# Revit family: RN 17011 Schrägfilter
name_source: partatom
category: Rohrzubehör
units: mm (PartAtom-declared; Revit-internal decimal feet)

## family parameters
Arbeitsebenenbasiert = Nein
Beim Laden mit Abzugskörper schneiden = Nein
Bemaßung runder Anschluss = Durchmesser verwenden
Gemeinsam genutzt = Nein
Immer vertikal = Ja
Teiletyp = Ventil - Zerlegung in

## types (7) — shared parameters
1.010.00.2 Blattnummer der Richtlinie = 17
1.010.00.3 Ausgabedatum (Monat) der Richtlinie = 201601
1.010.00.4 Herstellername = R. Nussbaum AG
1.010.00.5 Revisionsdatum der Datei = 20190528
1.010.00.6 Webadresse des Herstellers = http://www.nussbaum.ch
1.100.00.3 Sortiernummer für Anzeigereihenfolge = 9
1.100.00.4 Produktbezeichnung = Filterkombination, Filter und Schmutzfänger
1.960/3L.00.8 Link (URL) = https://www.nussbaum.ch
17.700.00.4 Armaturentyp = 1
17.700.00.7 Maximale Betriebstemperatur TB [°C] = 60
17.700.00.8 Maximaler Betriebsdruck (Arbeitsdruck) ps [1.0 · 105 Pa] = 16
Connector Visibility = Nein
EnclosingSpace Visibility = Nein
Hersteller = R. Nussbauzm AG
URL = https://www.nussbaum.ch

## per-type parameters (varying)
- DN 10: 1.800.00.3 TGA-Nummer=0090030000000000000000000000020070000000000000000100000000; 1.810.00.3 Hersteller-Bestellnummer=17011.03; 1.810.00.4 DATANORM-Nummer=17011.03; 1.810.00.5 StLB-Nummer=616.132; 1.810.00.6 GTIN-Nummer=7612945612618; 17.700.00.30 Produktbeschreibung=17011.03, Schrägfilter, DN=10, Rp=3/8; 17.700.00.5 Nennweite DN=10; 17.700.00.6 kvs-Wert [m3/h]=3; CONNECTOR0_DIAMETER_dX_0r=15 mm; CONNECTOR0_dX_00=35 mm; CONNECTOR0_dX_01=22 mm; CONNECTOR0_ref_dX=22 mm; CONNECTOR1_DIAMETER_dX_0r=15 mm; CONNECTOR1_dX_00=22 mm; CONNECTOR1_dX_01=35 mm; CONNECTOR1_ref_dX=22 mm; Modell=17011.03; R. Nussbaum AG 17011.03 de Visibility=Ja; R. Nussbaum AG 17011.04 de Visibility=Nein; R. Nussbaum AG 17011.05 de Visibility=Nein; R. Nussbaum AG 17011.06 de Visibility=Nein; R. Nussbaum AG 17011.07 de Visibility=Nein; R. Nussbaum AG 17011.08 de Visibility=Nein; R. Nussbaum AG 17011.09 de Visibility=Nein; Typenkommentare=SchrägfilterDN 10
- DN 15: 1.800.00.3 TGA-Nummer=0090030000000000000000000000020070000000000000000200000000; 1.810.00.3 Hersteller-Bestellnummer=17011.04; 1.810.00.4 DATANORM-Nummer=17011.04; 1.810.00.5 StLB-Nummer=616.133; 1.810.00.6 GTIN-Nummer=7612945612625; 17.700.00.30 Produktbeschreibung=17011.04, Schrägfilter, DN=15, Rp=½; 17.700.00.5 Nennweite DN=15; 17.700.00.6 kvs-Wert [m3/h]=6.3; CONNECTOR0_DIAMETER_dX_0r=15 mm; CONNECTOR0_dX_00=35 mm; CONNECTOR0_dX_01=22 mm; CONNECTOR0_ref_dX=22 mm; CONNECTOR1_DIAMETER_dX_0r=15 mm; CONNECTOR1_dX_00=22 mm; CONNECTOR1_dX_01=35 mm; CONNECTOR1_ref_dX=22 mm; Modell=17011.04; R. Nussbaum AG 17011.03 de Visibility=Nein; R. Nussbaum AG 17011.04 de Visibility=Ja; R. Nussbaum AG 17011.05 de Visibility=Nein; R. Nussbaum AG 17011.06 de Visibility=Nein; R. Nussbaum AG 17011.07 de Visibility=Nein; R. Nussbaum AG 17011.08 de Visibility=Nein; R. Nussbaum AG 17011.09 de Visibility=Nein; Typenkommentare=SchrägfilterDN 15
- DN 20: 1.800.00.3 TGA-Nummer=0090030000000000000000000000020070000000000000000300000000; 1.810.00.3 Hersteller-Bestellnummer=17011.05; 1.810.00.4 DATANORM-Nummer=17011.05; 1.810.00.5 StLB-Nummer=616.134; 1.810.00.6 GTIN-Nummer=7612945612632; 17.700.00.30 Produktbeschreibung=17011.05, Schrägfilter, DN=20, Rp=¾; 17.700.00.5 Nennweite DN=20; 17.700.00.6 kvs-Wert [m3/h]=13.4; CONNECTOR0_DIAMETER_dX_0r=20 mm; CONNECTOR0_dX_00=42 mm; CONNECTOR0_dX_01=27 mm; CONNECTOR0_ref_dX=27 mm; CONNECTOR1_DIAMETER_dX_0r=20 mm; CONNECTOR1_dX_00=28 mm; CONNECTOR1_dX_01=43 mm; CONNECTOR1_ref_dX=28 mm; Modell=17011.05; R. Nussbaum AG 17011.03 de Visibility=Nein; R. Nussbaum AG 17011.04 de Visibility=Nein; R. Nussbaum AG 17011.05 de Visibility=Ja; R. Nussbaum AG 17011.06 de Visibility=Nein; R. Nussbaum AG 17011.07 de Visibility=Nein; R. Nussbaum AG 17011.08 de Visibility=Nein; R. Nussbaum AG 17011.09 de Visibility=Nein; Typenkommentare=SchrägfilterDN 20
- DN 25: 1.800.00.3 TGA-Nummer=0090030000000000000000000000020070000000000000000400000000; 1.810.00.3 Hersteller-Bestellnummer=17011.06; 1.810.00.4 DATANORM-Nummer=17011.06; 1.810.00.5 StLB-Nummer=616.135; 1.810.00.6 GTIN-Nummer=7612945612649; 17.700.00.30 Produktbeschreibung=17011.06, Schrägfilter, DN=25, Rp=1; 17.700.00.5 Nennweite DN=25; 17.700.00.6 kvs-Wert [m3/h]=21.6; CONNECTOR0_DIAMETER_dX_0r=25 mm  [stored 0.082021 ft]; CONNECTOR0_dX_00=50 mm; CONNECTOR0_dX_01=33 mm; CONNECTOR0_ref_dX=33 mm; CONNECTOR1_DIAMETER_dX_0r=25 mm  [stored 0.082021 ft]; CONNECTOR1_dX_00=33 mm; CONNECTOR1_dX_01=50 mm; CONNECTOR1_ref_dX=33 mm; Modell=17011.06; R. Nussbaum AG 17011.03 de Visibility=Nein; R. Nussbaum AG 17011.04 de Visibility=Nein; R. Nussbaum AG 17011.05 de Visibility=Nein; R. Nussbaum AG 17011.06 de Visibility=Ja; R. Nussbaum AG 17011.07 de Visibility=Nein; R. Nussbaum AG 17011.08 de Visibility=Nein; R. Nussbaum AG 17011.09 de Visibility=Nein; Typenkommentare=SchrägfilterDN 25
- DN 32: 1.800.00.3 TGA-Nummer=0090030000000000000000000000020070000000000000000500000000; 1.810.00.3 Hersteller-Bestellnummer=17011.07; 1.810.00.4 DATANORM-Nummer=17011.07; 1.810.00.5 StLB-Nummer=616.136; 1.810.00.6 GTIN-Nummer=7612945612656; 17.700.00.30 Produktbeschreibung=17011.07, Schrägfilter, DN=32, Rp=1¼; 17.700.00.5 Nennweite DN=32; 17.700.00.6 kvs-Wert [m3/h]=37; CONNECTOR0_DIAMETER_dX_0r=32 mm; CONNECTOR0_dX_00=57 mm; CONNECTOR0_dX_01=39 mm; CONNECTOR0_ref_dX=39 mm; CONNECTOR1_DIAMETER_dX_0r=32 mm; CONNECTOR1_dX_00=38 mm; CONNECTOR1_dX_01=58 mm; CONNECTOR1_ref_dX=38 mm; Modell=17011.07; R. Nussbaum AG 17011.03 de Visibility=Nein; R. Nussbaum AG 17011.04 de Visibility=Nein; R. Nussbaum AG 17011.05 de Visibility=Nein; R. Nussbaum AG 17011.06 de Visibility=Nein; R. Nussbaum AG 17011.07 de Visibility=Ja; R. Nussbaum AG 17011.08 de Visibility=Nein; R. Nussbaum AG 17011.09 de Visibility=Nein; Typenkommentare=SchrägfilterDN 32
- DN 40: 1.800.00.3 TGA-Nummer=0090030000000000000000000000020070000000000000000600000000; 1.810.00.3 Hersteller-Bestellnummer=17011.08; 1.810.00.4 DATANORM-Nummer=17011.08; 1.810.00.5 StLB-Nummer=616.137; 1.810.00.6 GTIN-Nummer=7612945612663; 17.700.00.30 Produktbeschreibung=17011.08, Schrägfilter, DN=40, Rp=1½; 17.700.00.5 Nennweite DN=40; 17.700.00.6 kvs-Wert [m3/h]=51.6; CONNECTOR0_DIAMETER_dX_0r=40 mm; CONNECTOR0_dX_00=65 mm; CONNECTOR0_dX_01=46 mm; CONNECTOR0_ref_dX=46 mm; CONNECTOR1_DIAMETER_dX_0r=40 mm; CONNECTOR1_dX_00=46 mm; CONNECTOR1_dX_01=65 mm; CONNECTOR1_ref_dX=46 mm; Modell=17011.08; R. Nussbaum AG 17011.03 de Visibility=Nein; R. Nussbaum AG 17011.04 de Visibility=Nein; R. Nussbaum AG 17011.05 de Visibility=Nein; R. Nussbaum AG 17011.06 de Visibility=Nein; R. Nussbaum AG 17011.07 de Visibility=Nein; R. Nussbaum AG 17011.08 de Visibility=Ja; R. Nussbaum AG 17011.09 de Visibility=Nein; Typenkommentare=SchrägfilterDN 40
- DN 50: 1.800.00.3 TGA-Nummer=0090030000000000000000000000020070000000000000000700000000; 1.810.00.3 Hersteller-Bestellnummer=17011.09; 1.810.00.4 DATANORM-Nummer=17011.09; 1.810.00.5 StLB-Nummer=616.138; 1.810.00.6 GTIN-Nummer=7612945612670; 17.700.00.30 Produktbeschreibung=17011.09, Schrägfilter, DN=50, Rp=2; 17.700.00.5 Nennweite DN=50; 17.700.00.6 kvs-Wert [m3/h]=81; CONNECTOR0_DIAMETER_dX_0r=50 mm; CONNECTOR0_dX_00=75 mm; CONNECTOR0_dX_01=51 mm; CONNECTOR0_ref_dX=51 mm; CONNECTOR1_DIAMETER_dX_0r=50 mm; CONNECTOR1_dX_00=51 mm; CONNECTOR1_dX_01=75 mm; CONNECTOR1_ref_dX=51 mm; Modell=17011.09; R. Nussbaum AG 17011.03 de Visibility=Nein; R. Nussbaum AG 17011.04 de Visibility=Nein; R. Nussbaum AG 17011.05 de Visibility=Nein; R. Nussbaum AG 17011.06 de Visibility=Nein; R. Nussbaum AG 17011.07 de Visibility=Nein; R. Nussbaum AG 17011.08 de Visibility=Nein; R. Nussbaum AG 17011.09 de Visibility=Ja; Typenkommentare=SchrägfilterDN 50

note: [stored X ft] marks values corroborated as IEEE doubles in the binary element streams (Revit-internal decimal feet)

## geometry (parser evidence)
native form markers: Sweep x1
no freeform markers — native parametric forms only
